# Revit family: Shower-Showerhead-KOHLER-K-26296IN_1
name_source: partatom
category: Plumbing Fixtures
revit_build: Autodesk Revit 2017 (Build: 20160225_1515(x64)
units: mm (PartAtom-declared; Revit-internal decimal feet)

## family parameters
Cut with Voids When Loaded = No
Host = Face
OmniClass Number = 23.31.17.00
OmniClass Title = Showers
Part Type = Normal
Room Calculation Point = No
Round Connector Dimension = Use Diameter
Shared = No

## types (6) — shared parameters
ADA Compliant = No
Assembly Code = D2010700
CW Connection = No
Cold Water Inlet = Cold Water Inlet
Date Modified = 02/02/2021
Default Elevation = 0"
Description = 2F MEDIUM OBLONG KATALYST / CASCADE-2.5 GPM
Drain Included = No
Flow Rate = 3 GPM
HW Connection = Yes
Height = 3 7/16"
Hot Water Inlet = Hot Water Inlet
Length = 8"
Manufacturer = KOHLER Co.
Master Format 2014 = 22 42 23
Master Format 2014 Name = Residential Showers
Material = Plastic
Panel Thickness = 0"
Pressure = 80.00 psi
Tempered Water Inlet = Tempered Water Inlet
URL = https://www.kohler.co.in
Vent Connection = No
Waste Connection = No
Waste Water Outlet = Waste Water Outlet
WaterSense Certified = No
Width = 13 7/8"

## per-type parameters (varying)
| type | Finish | Model | Type |
| AF- Flange Gold | KOHLER-Plastic-AF-Vibrant_French_Gold | K-26296IN-AF | 1 |
| BL- Matte Black | Kohler-Plastic-BL-Matte_Black | K-26296IN-BL | 2 |
| BN- Brushed Nickel | KOHLER-Plastic-BN-Vibrant_Brushed_Nickel | K-26296IN-BN | 3 |
| BV- Brushed Bronze | Kohler-Plastic-BV-Vibrant-Brushed-Bronze | K-26296IN-BV | 4 |
| CP- Polished Chrome | Kohler-Plastic-CP-Polished_Chrome | K-26296IN-CP | 5 |
| RGD- Rose Gold | Kohler-Plastic-RGD-Rose_Gold | K-26296IN-RGD | 6 |

## geometry (parser evidence)
native form markers: Sweep x4
no freeform markers — native parametric forms only
